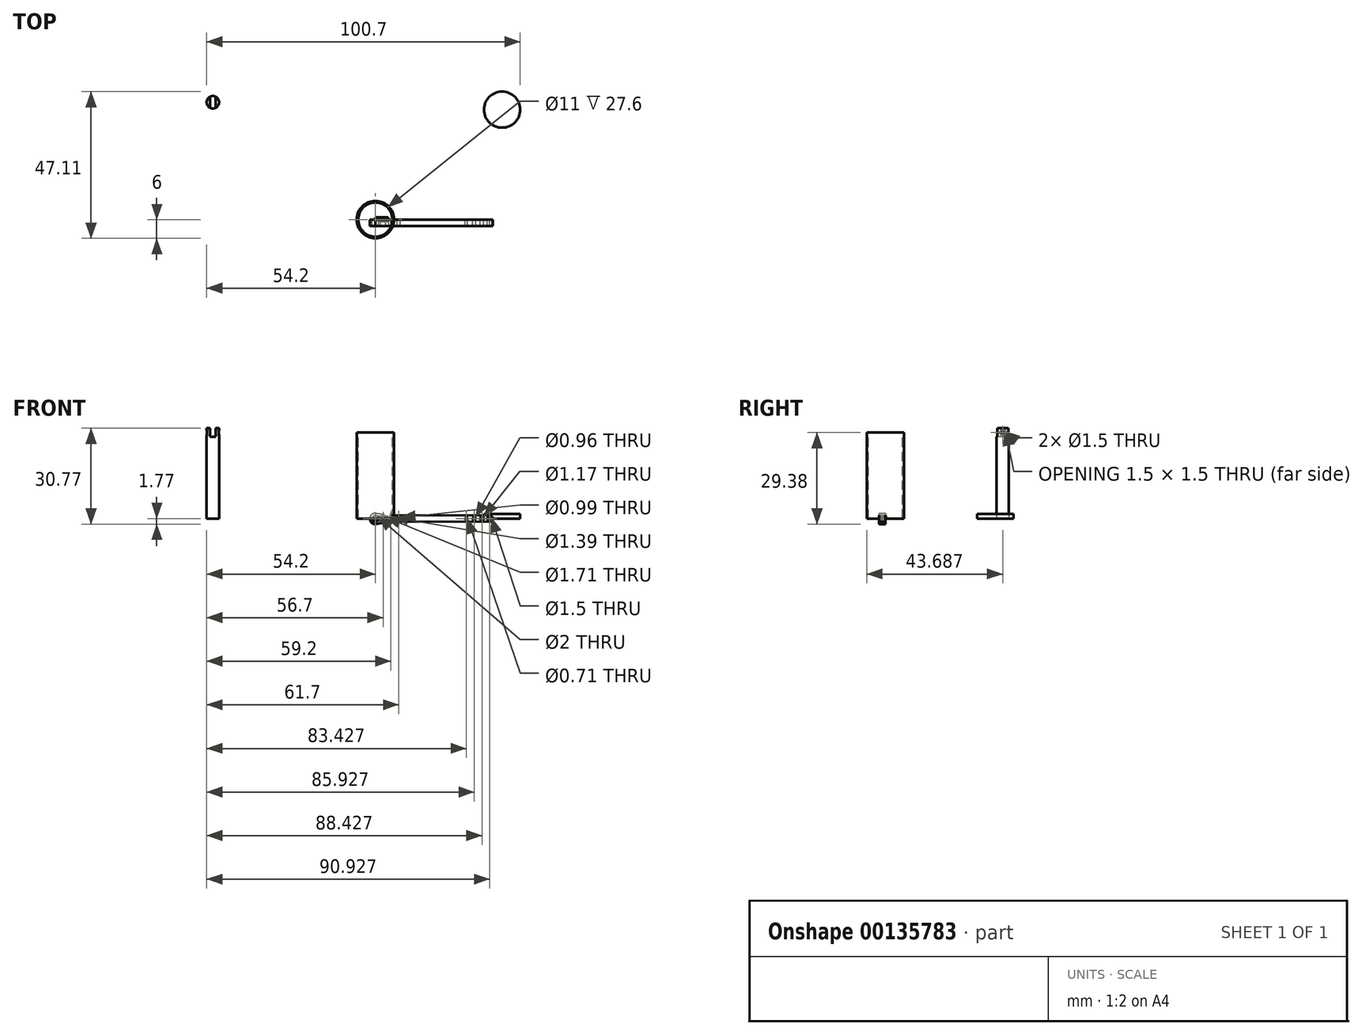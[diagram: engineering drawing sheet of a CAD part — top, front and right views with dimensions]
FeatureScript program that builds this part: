
annotation { "Feature Type Name" : "Feature", "Feature Type Description" : "" }
export const myFeature = defineFeature(function(context is Context, id is Id, definition is map)
    precondition{}
    {
        {
            var Q0;
            Q0=qCreatedBy(makeId("Top.planeOp"),FACE);
            var sketch = newSketch(context, id + "F0", { "sketchPlane" : qUnion([Q0])});
            skCircle(sketch, "E0", {"center": v(0, 0) * mm, "radius": 6 * mm});
            skSolve(sketch);
        }
        {
            var Q0;
            Q0=sQuery(id+"F0.wireOp",EDGE,"E0");
            extrude(context, id + "F1", {"bodyType" : ToolBodyType.SURFACE, "surfaceEntities" : qUnion([Q0]), "depth" : 27.6 * mm});
        }
        {
            var Q0;
            Q0=qCreatedBy(makeId("Top.planeOp"),FACE);
            var sketch = newSketch(context, id + "F2", { "sketchPlane" : qUnion([Q0])});
            skCircle(sketch, "E1", {"center": v(40.7, 35.31) * mm, "radius": 5.8 * mm});
            skSolve(sketch);
        }
        {
            var Q0;
            Q0 = qSketchRegion(id + "F2", true);
            extrude(context, id + "F3", {"entities" : qUnion([Q0]), "depth" : 1.5 * mm});
        }
        {
            var Q0;
            Q0=qCreatedBy(makeId("Top.planeOp"),FACE);
            var sketch = newSketch(context, id + "F4", { "sketchPlane" : qUnion([Q0])});
            skCircle(sketch, "E2", {"center": v(-52.2, 37.69) * mm, "radius": 2 * mm});
            skSolve(sketch);
        }
        {
            var Q0;
            Q0 = qSketchRegion(id + "F4", true);
            extrude(context, id + "F5", {"entities" : qUnion([Q0]), "depth" : 29 * mm});
        }
        {
            var Q0;
            Q0=makeQuery(id+"F5.opExtrude","CAP_FACE",FACE,{"disambiguationData":[OSD([sQuery(id+"F4.wireOp",EDGE,"E2")])],"isStart":false});
            var sketch = newSketch(context, id + "F6", { "sketchPlane" : qUnion([Q0])});
            skLineSegment(sketch, "E3.bottom", {"start": v(-53.07, 39.84) * mm, "end": v(-51.32, 39.84) * mm});
            skLineSegment(sketch, "E3.top", {"start": v(-53.07, 35.35) * mm, "end": v(-51.32, 35.35) * mm});
            skLineSegment(sketch, "E3.left", {"start": v(-53.07, 39.84) * mm, "end": v(-53.07, 35.35) * mm});
            skLineSegment(sketch, "E3.right", {"start": v(-51.32, 39.84) * mm, "end": v(-51.32, 35.35) * mm});
            skLineSegment(sketch, "E4", {"start": v(-52.2, 40.3) * mm, "end": v(-52.2, 35.07) * mm, "construction": true});
            skCircle(sketch, "E5.0", {"center": v(-52.2, 37.69) * mm, "radius": 2 * mm});
            skLineSegment(sketch, "E6", {"start": v(-54.78, 37.69) * mm, "end": v(-49.46, 37.69) * mm, "construction": true});
            skSolve(sketch);
        }
        {
            var Q0;
            {var subQ0=sQuery(id+"F6.wireOp",EDGE,"E5.0");var subQ1=sQuery(id+"F6.wireOp",EDGE,"E3.left");var subQ2=makeQuery(id+"F6.imprint","INTERSECT",VERTEX,{"disambiguationData":[OD(0.0)],"derivedFrom":[subQ1,subQ0]});Q0=makeQuery(id+"F6.imprint","IMPRINT",FACE,{"disambiguationData":[TD([[makeQuery(id+"F6.imprint","IMPRINT",EDGE,{"disambiguationData":[TD([[subQ2,-1.0]])],"derivedFrom":subQ1}),1.0]])]});}
            extrude(context, id + "F7", {"entities" : qUnion([Q0]), "operationType" : NewBodyOperationType.REMOVE, "oppositeDirection" : true, "depth" : 2.78 * mm});
        }
        {
            var Q0;
            Q0=makeQuery(id+"F0.imprint","IMPRINT",FACE,{"disambiguationData":[TD([[makeQuery(id+"F0.imprint","IMPRINT",EDGE,{"derivedFrom":sQuery(id+"F0.wireOp",EDGE,"E0")}),1.0]])]});
            extrude(context, id + "F8", {"entities" : qUnion([Q0]), "depth" : 27.6 * mm});
        }
        {
            var Q0;
            Q0=makeQuery(id+"F8.opExtrude","CAP_FACE",FACE,{"disambiguationData":[OSD([sQuery(id+"F0.wireOp",EDGE,"E0")])],"isStart":false});
            var sketch = newSketch(context, id + "F9", { "sketchPlane" : qUnion([Q0])});
            skCircle(sketch, "E7", {"center": v(0, 0) * mm, "radius": 5.5 * mm});
            skSolve(sketch);
        }
        {
            var Q0;
            Q0=makeQuery(id+"F9.imprint","IMPRINT",FACE,{"disambiguationData":[TD([[makeQuery(id+"F9.imprint","IMPRINT",EDGE,{"derivedFrom":sQuery(id+"F9.wireOp",EDGE,"E7")}),1.0]])]});
            extrude(context, id + "F10", {"entities" : qUnion([Q0]), "operationType" : NewBodyOperationType.REMOVE, "oppositeDirection" : true, "depth" : 27.6 * mm});
        }
        {
            var Q0;
            Q0=qCreatedBy(makeId("Front.planeOp"),FACE);
            var sketch = newSketch(context, id + "F11", { "sketchPlane" : qUnion([Q0])});
            skArc(sketch, "E8", {"start": v(0, 1.77) * mm, "mid": v(-1.77, 0) * mm, "end": v(0, -1.77) * mm});
            skArc(sketch, "E9", {"start": v(36.66, -1) * mm, "mid": v(37.73, -0.04) * mm, "end": v(36.73, 1) * mm});
            skArc(sketch, "E10", {"start": v(0, 1.77) * mm, "mid": v(2.58, 1.41) * mm, "end": v(5.17, 1.18) * mm});
            skArc(sketch, "E11", {"start": v(5.25, -0.97) * mm, "mid": v(2.61, -1.3) * mm, "end": v(0, -1.77) * mm});
            skCircle(sketch, "E12", {"center": v(0, 0) * mm, "radius": 1 * mm});
            skCircle(sketch, "E13", {"center": v(36.73, 0) * mm, "radius": 0.75 * mm});
            skLineSegment(sketch, "E14", {"start": v(5.17, 1.18) * mm, "end": v(36.73, 1) * mm});
            skLineSegment(sketch, "E15", {"start": v(36.66, -1) * mm, "end": v(5.25, -0.97) * mm});
            skCircle(sketch, "E16", {"center": v(2.5, 0) * mm, "radius": 0.86 * mm});
            skCircle(sketch, "E17", {"center": v(5, 0) * mm, "radius": 0.7 * mm});
            skCircle(sketch, "E18", {"center": v(7.5, 0) * mm, "radius": 0.5 * mm});
            skCircle(sketch, "E19", {"center": v(34.23, 0) * mm, "radius": 0.58 * mm});
            skCircle(sketch, "E20", {"center": v(31.73, 0) * mm, "radius": 0.48 * mm});
            skCircle(sketch, "E21", {"center": v(29.23, 0) * mm, "radius": 0.36 * mm});
            skSolve(sketch);
        }
        {
            var Q0;
            Q0=makeQuery(id+"F11.imprint","IMPRINT",FACE,{"disambiguationData":[TD([[makeQuery(id+"F11.imprint","IMPRINT",EDGE,{"derivedFrom":sQuery(id+"F11.wireOp",EDGE,"E8")}),1.0]])]});
            extrude(context, id + "F12", {"entities" : qUnion([Q0]), "depth" : 2 * mm});
        }
        {
            var Q0;
            Q0=qCreatedBy(makeId("Right.planeOp"),FACE);
            var sketch = newSketch(context, id + "F13", { "sketchPlane" : qUnion([Q0])});
            skCircle(sketch, "E22", {"center": v(0, 0) * mm, "radius": 0.75 * mm});
            skSolve(sketch);
        }
        {
            var Q0;
            Q0 = qSketchRegion(id + "F13", true);
            extrude(context, id + "F14", {"entities" : qUnion([Q0]), "depth" : 4 * mm});
        }
        {
            var Q0;
            Q0=qCreatedBy(makeId("Right.planeOp"),FACE);
            var sketch = newSketch(context, id + "F15", { "sketchPlane" : qUnion([Q0])});
            skCircle(sketch, "E23", {"center": v(37.69, 27.61) * mm, "radius": 0.75 * mm});
            skLineSegment(sketch, "E24", {"start": v(35.58, 27.61) * mm, "end": v(40.58, 27.61) * mm, "construction": true});
            skLineSegment(sketch, "E25", {"start": v(37.69, 31.55) * mm, "end": v(37.69, 26.5) * mm, "construction": true});
            skLineSegment(sketch, "E26.0", {"start": v(35.89, 26.22) * mm, "end": v(35.89, 29) * mm});
            skLineSegment(sketch, "E27.0", {"start": v(35.89, 29) * mm, "end": v(39.49, 29) * mm});
            skSolve(sketch);
        }
        {
            var Q0;
            Q0=makeQuery(id+"F15.imprint","IMPRINT",FACE,{"disambiguationData":[TD([[makeQuery(id+"F15.imprint","IMPRINT",EDGE,{"derivedFrom":sQuery(id+"F15.wireOp",EDGE,"E23")}),1.0]])]});
            extrude(context, id + "F16", {"entities" : qUnion([Q0]), "operationType" : NewBodyOperationType.REMOVE, "endBound" : BoundingType.THROUGH_ALL, "oppositeDirection" : true, "depth" : 25 * mm});
        }
    });
